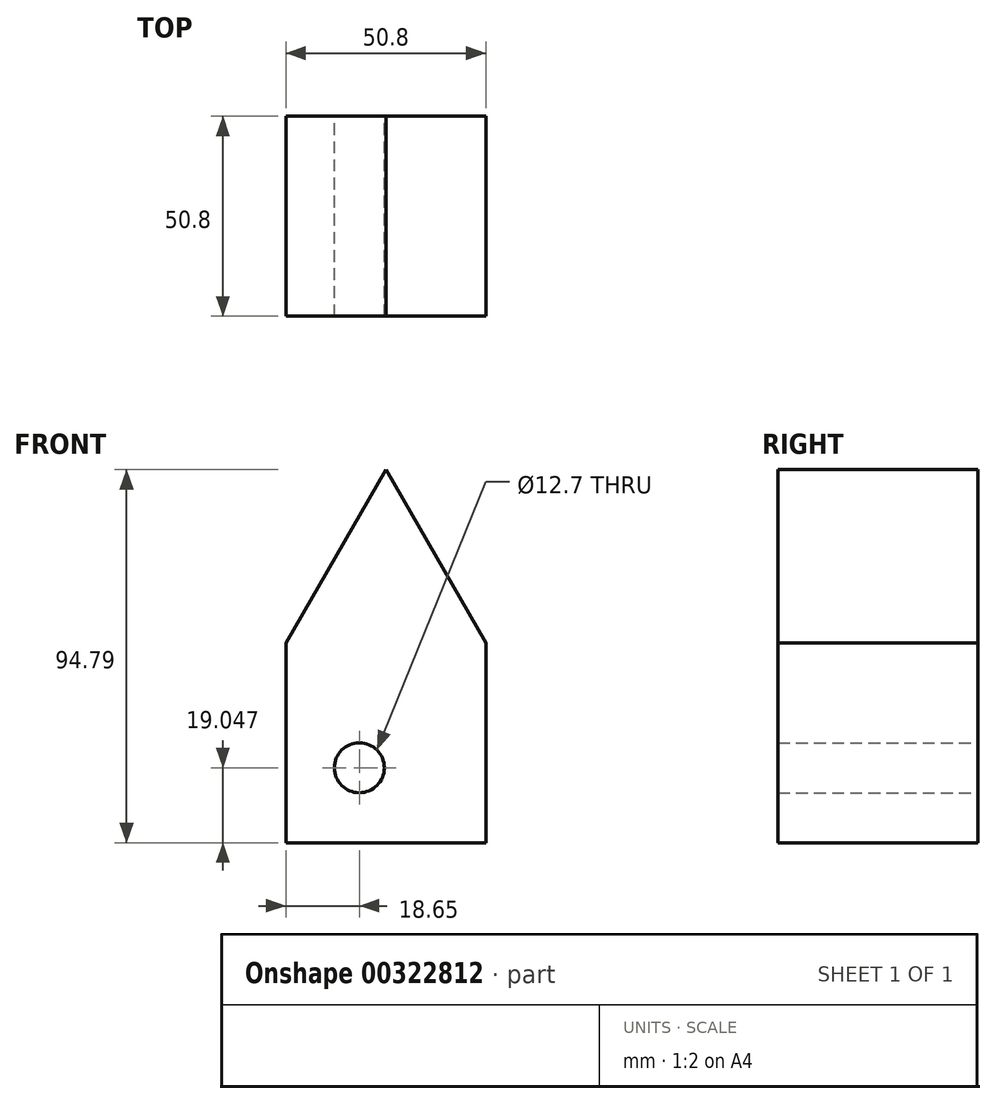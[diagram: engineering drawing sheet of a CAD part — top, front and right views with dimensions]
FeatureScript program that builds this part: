
annotation { "Feature Type Name" : "Feature", "Feature Type Description" : "" }
export const myFeature = defineFeature(function(context is Context, id is Id, definition is map)
    precondition{}
    {
        {
            var Q0;
            Q0=qCreatedBy(makeId("Front.planeOp"),FACE);
            var sketch = newSketch(context, id + "F0", { "sketchPlane" : qUnion([Q0])});
            skLineSegment(sketch, "E0.top", {"start": v(-18.65, -31.51) * mm, "end": v(32.15, -31.51) * mm});
            skLineSegment(sketch, "E0.left", {"start": v(-18.65, 19.29) * mm, "end": v(-18.65, -31.51) * mm});
            skLineSegment(sketch, "E0.right", {"start": v(32.15, 19.29) * mm, "end": v(32.15, -31.51) * mm});
            skLineSegment(sketch, "E1", {"start": v(-18.65, 19.29) * mm, "end": v(6.75, 63.28) * mm});
            skPoint(sketch, "E2.end.orphan", {"position": v(10.22, 63.28) * mm});
            skLineSegment(sketch, "E3", {"start": v(6.75, 63.28) * mm, "end": v(32.15, 19.29) * mm});
            skCircle(sketch, "E4", {"center": v(0, -12.46) * mm, "radius": 6.35 * mm});
            skSolve(sketch);
        }
        {
            var Q0;
            Q0 = qSketchRegion(id + "F0", true);
            extrude(context, id + "F1", {"entities" : qUnion([Q0]), "depth" : 50.8 * mm});
        }
    });
